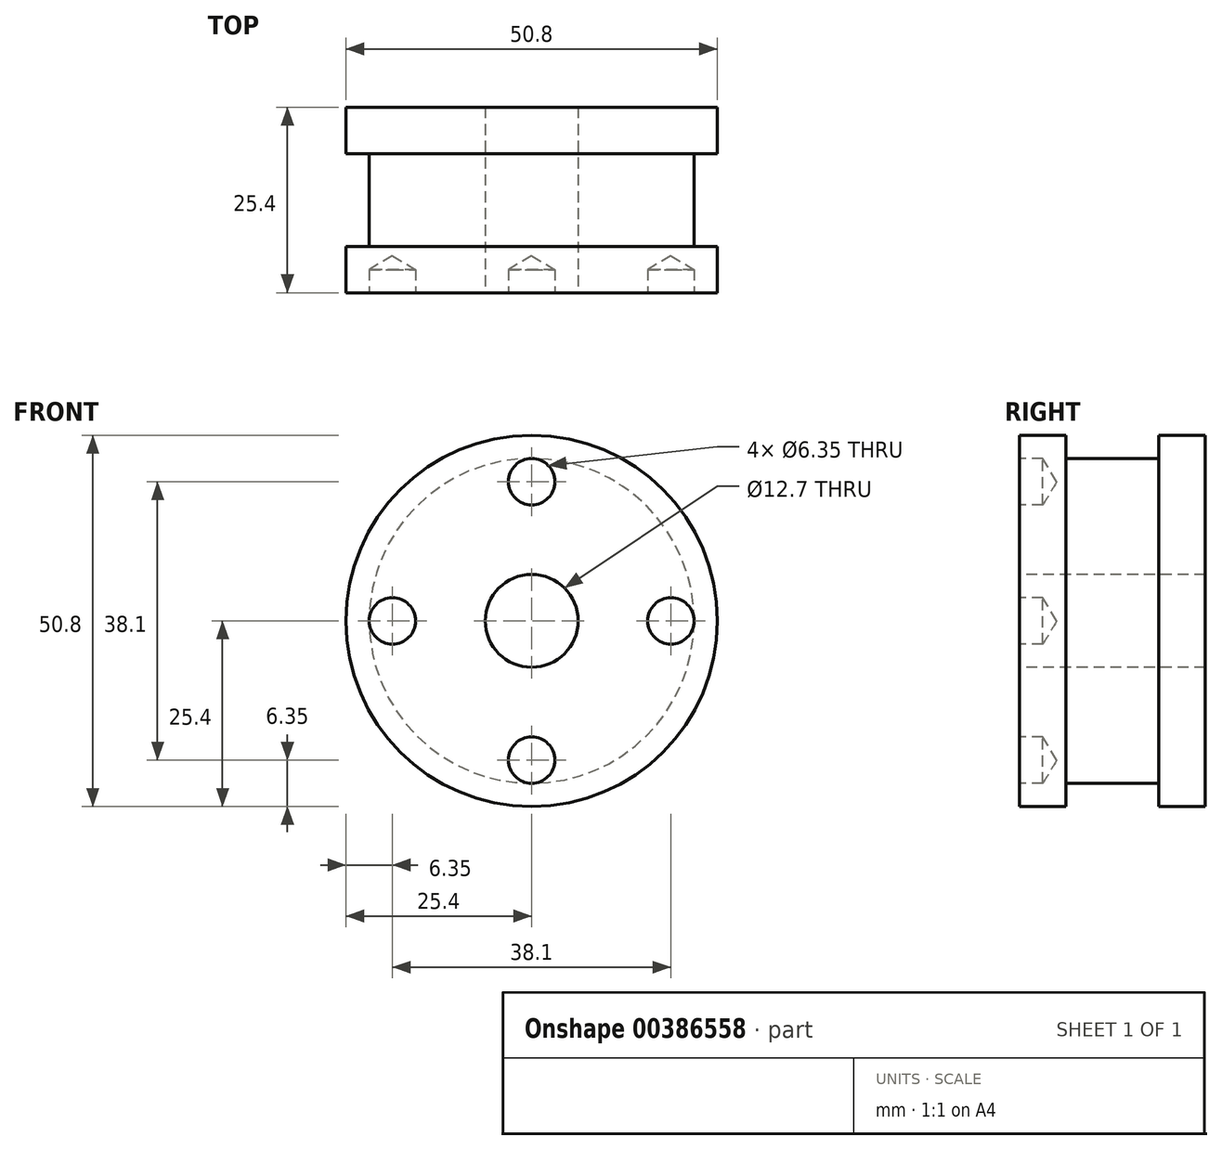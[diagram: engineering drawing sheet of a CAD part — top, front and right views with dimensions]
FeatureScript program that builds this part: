
annotation { "Feature Type Name" : "Feature", "Feature Type Description" : "" }
export const myFeature = defineFeature(function(context is Context, id is Id, definition is map)
    precondition{}
    {
        {
            var Q0;
            Q0=qCreatedBy(makeId("Front.planeOp"),FACE);
            var sketch = newSketch(context, id + "F0", { "sketchPlane" : qUnion([Q0])});
            skCircle(sketch, "E0", {"center": v(0, 0) * mm, "radius": 25.4 * mm});
            skSolve(sketch);
        }
        {
            var Q0;
            Q0 = qSketchRegion(id + "F0", true);
            extrude(context, id + "F1", {"entities" : qUnion([Q0]), "depth" : 6.35 * mm});
        }
        {
            var Q0;
            Q0=makeQuery(id+"F1.opExtrude","CAP_FACE",FACE,{"disambiguationData":[OSD([sQuery(id+"F0.wireOp",EDGE,"E0")])],"isStart":false});
            var sketch = newSketch(context, id + "F2", { "sketchPlane" : qUnion([Q0])});
            skCircle(sketch, "E1", {"center": v(0, 0) * mm, "radius": 22.23 * mm});
            skSolve(sketch);
        }
        {
            var Q0;
            Q0 = qSketchRegion(id + "F2", true);
            extrude(context, id + "F3", {"entities" : qUnion([Q0]), "operationType" : NewBodyOperationType.ADD, "depth" : 12.7 * mm});
        }
        {
            var Q0;
            Q0=makeQuery(id+"F3.opExtrude","CAP_FACE",FACE,{"disambiguationData":[OSD([sQuery(id+"F2.wireOp",EDGE,"E1")])],"isStart":false});
            var sketch = newSketch(context, id + "F4", { "sketchPlane" : qUnion([Q0])});
            skCircle(sketch, "E2", {"center": v(0, 0) * mm, "radius": 25.4 * mm});
            skSolve(sketch);
        }
        {
            var Q0;
            Q0 = qSketchRegion(id + "F4", true);
            extrude(context, id + "F5", {"entities" : qUnion([Q0]), "operationType" : NewBodyOperationType.ADD, "depth" : 6.35 * mm});
        }
        {
            var Q0;
            Q0=makeQuery(id+"F5.opExtrude","CAP_FACE",FACE,{"disambiguationData":[OSD([sQuery(id+"F4.wireOp",EDGE,"E2")])],"isStart":false});
            var sketch = newSketch(context, id + "F6", { "sketchPlane" : qUnion([Q0])});
            skPoint(sketch, "E3", {"position": v(-19.05, 0) * mm});
            skPoint(sketch, "E4", {"position": v(19.05, 0) * mm});
            skPoint(sketch, "E5", {"position": v(0, 19.05) * mm});
            skPoint(sketch, "E6", {"position": v(0, -19.05) * mm});
            skPoint(sketch, "E7", {"position": v(0, 0) * mm});
            skSolve(sketch);
        }
        {
            var Q0;
            Q0=sQuery(id+"F6.wireOp",VERTEX,"E3");
            var Q1;
            Q1=sQuery(id+"F6.wireOp",VERTEX,"E6");
            var Q2;
            Q2=sQuery(id+"F6.wireOp",VERTEX,"E4");
            var Q3;
            Q3=sQuery(id+"F6.wireOp",VERTEX,"E5");
            var Q4;
            Q4=makeQuery(id+"F1.opExtrude","SWEPT_BODY",BODY,{"disambiguationData":[OSD([sQuery(id+"F0.wireOp",EDGE,"E0")])]});
            hole(context, id + "F7", {"style" : HoleStyle.SIMPLE, "endStyle" : HoleEndStyle.BLIND, "holeDiameter" : 6.35 * mm, "holeDepth" : 3.17 * mm, "isTappedThrough" : true, "tappedDepth" : 12.7 * mm, "tapClearance" : 3, "startFromSketch" : true, "locations" : qUnion([Q0, Q1, Q2, Q3]), "scope" : qUnion([Q4])});
        }
        {
            var Q0;
            Q0=makeQuery(id+"F5.opExtrude","CAP_FACE",FACE,{"disambiguationData":[OSD([sQuery(id+"F4.wireOp",EDGE,"E2")])],"isStart":false});
            var sketch = newSketch(context, id + "F8", { "sketchPlane" : qUnion([Q0])});
            skPoint(sketch, "E8", {"position": v(0, 0) * mm});
            skSolve(sketch);
        }
        {
            var Q0;
            Q0=sQuery(id+"F8.wireOp",VERTEX,"E8");
            var Q1;
            Q1=makeQuery(id+"F1.opExtrude","SWEPT_BODY",BODY,{"disambiguationData":[OSD([sQuery(id+"F0.wireOp",EDGE,"E0")])]});
            hole(context, id + "F9", {"style" : HoleStyle.SIMPLE, "endStyle" : HoleEndStyle.THROUGH, "holeDiameter" : 12.7 * mm, "isTappedThrough" : true, "tappedDepth" : 12.7 * mm, "tapClearance" : 3, "startFromSketch" : true, "locations" : qUnion([Q0]), "scope" : qUnion([Q1])});
        }
    });
